# Revit family: Doors_Industrial_Wayne-Dalton_Roll-Up-Sheet-Doors-Model-780-CD_
name_source: partatom
category: Specialty Equipment
units: mm (PartAtom-declared; Revit-internal decimal feet)

## family parameters
Always vertical = Yes
Cut with Voids When Loaded = No
Host = Wall
OmniClass Number = 23.30.10.21.34
OmniClass Title = Industrial Doors
Part Type = Normal
Room Calculation Point = No
Round Connector Dimension = Use Diameter
Shared = No

## types (2) — shared parameters
Description = MODEL 780CD COMMERCIAL ROLLING SHEET DOOR
Finish Material = Metal - Wayne Dalton - Galvanized Steel
Manufacturer = Wayne Dalton
Model = 780CD
Product Guid = 43a41605-6605-48ef-871c-127e65c06177
Product Page URL = https://www.wayne-dalton.com
Product data url = https://www.bimobject.com
Slat Height = 10"
URL = https://www.wayne-dalton.com
Wall Closure = By host

## type names
- ‏​Manual push-up
- Chain Hoist
type visibility flags (boolean, named after types; folded from table):
- ‏​Manual push-up: Yes: (none)
- Chain Hoist: Yes: Chain Hoist

## geometry (parser evidence)
native form markers: Sweep x10
no freeform markers — native parametric forms only
